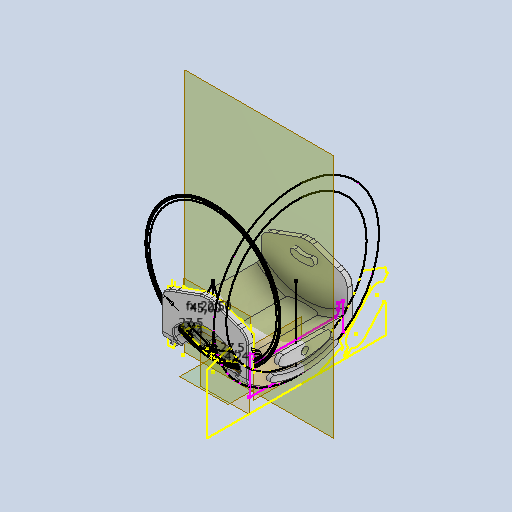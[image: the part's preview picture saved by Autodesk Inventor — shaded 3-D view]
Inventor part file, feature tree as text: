
AUTODESK INVENTOR PART (.ipt)
format: ipt  version: 2022 (Build 260153000, 153)  size: 1,173,504 bytes
history: native  units: mm
features: reference x42, other x22, extrude x21, sketch x20, projected_geometry x20, fillet x14, mirror x1
ambient origin geometry x8: Origin, YZ Plane, XZ Plane, XY Plane, X Axis, Y Axis, Z Axis, Center Point
bodies: Body1 (feature_tree)
feature tree (140):
  other  "Твердое тело1"
  extrude  "Выдавливание1"  Depth=1.2mm
  sketch  "Эскиз2"
  other  "РабПлоскость11"
  extrude  "Выдавливание2"  Depth=3.490659mm
  sketch  "Эскиз4"
  extrude  "Выдавливание3"  Depth=3.490659mm
  extrude  "Выдавливание4"  Depth=0.2mm
  other  "РабПлоскость2"
  other  "РабПлоскость3"
  extrude  "Выдавливание5"  Depth=2.7mm TaperAngle=0.0deg
  extrude  "Выдавливание6"  Depth=0.05mm
  fillet  "Сопряжение6"  [1 undecoded]
  fillet  "Сопряжение8"  [1 undecoded]
  extrude  "Выдавливание9"  Depth=1.8mm TaperAngle=0.0deg
  other  "РабПлоскость6"
  extrude  "Выдавливание11"  Depth=1.0mm
  other  "РабПлоскость5"
  sketch  "Эскиз15"
  extrude  "Выдавливание12"  TaperAngle=45.0deg  [1 undecoded]
  other  "РабПлоскость7"
  extrude  "Выдавливание13"  TaperAngle=22.5deg  [1 undecoded]
  extrude  "Выдавливание14"  Depth=27.5mm
  extrude  "Выдавливание15"  Depth=27.5mm
  extrude  "Выдавливание16"  Depth=4.24mm
  sketch  "Эскиз22"
  other  "РабПлоскость4"
  extrude  "Выдавливание17"  Depth=4.24mm
  extrude  "Выдавливание18"  Depth=42.5mm TaperAngle=0.0deg
  fillet  "Сопряжение12"  Radius=2.7mm
  other  "РабПлоскость8"
  fillet  "Сопряжение13"  Radius=0.2mm
  extrude  "Выдавливание20"  Depth=8.0mm TaperAngle=0.0deg
  fillet  "Сопряжение14"  Radius=4.0mm
  fillet  "Сопряжение15"  Radius=0.5mm
  other  "РабПлоскость9"
  mirror  "Зеркальное отражение1"
  extrude  "Выдавливание21"  Depth=4.363323mm
  fillet  "Сопряжение17"  Radius=4.363323mm
  fillet  "Сопряжение20"  Radius=0.3mm
  fillet  "Сопряжение21"  Radius=1.0mm
  extrude  "Выдавливание25"  Depth=0.8mm
  extrude  "Выдавливание26"  Depth=5.0mm
  fillet  "Сопряжение23"  Radius=10.0mm
  fillet  "Сопряжение24"  Radius=40.0mm
  fillet  "Сопряжение27"  Radius=40.0mm
  fillet  "Сопряжение28"  Radius=4.3mm
  extrude  "Выдавливание27"  Depth=1.3mm TaperAngle=0.0deg
  fillet  "Сопряжение29"  Radius=1.8mm
  extrude  "Выдавливание28"  Depth=2.0mm TaperAngle=0.0deg
  sketch  "Эскиз1"
  reference  "Ссылка1"
  reference  "Ссылка2"
  reference  "Ссылка3"
  reference  "Ссылка4"
  reference  "Ссылка5"
  reference  "Ссылка6"
  reference  "Ссылка7"
  reference  "Ссылка8"
  reference  "Ссылка9"
  reference  "Ссылка10"
  reference  "Ссылка11"
  reference  "Ссылка12"
  reference  "Ссылка13"
  reference  "Ссылка14"
  projected_geometry  "Спроецированная петля1"
  reference  "Ссылка15"
  reference  "Ссылка16"
  reference  "Ссылка17"
  reference  "Ссылка18"
  reference  "Ссылка19"
  reference  "Ссылка20"
  sketch  "Эскиз5"
  projected_geometry  "Спроецированная петля2"
  sketch  "Эскиз6"
  projected_geometry  "Спроецированная петля3"
  sketch  "Эскиз8"
  reference  "Ссылка29"
  reference  "Ссылка31"
  projected_geometry  "Спроецированная петля5"
  projected_geometry  "Спроецированная петля6"
  reference  "Ссылка32"
  reference  "Ссылка33"
  sketch  "Эскиз9"
  projected_geometry  "Спроецированная петля7"
  sketch  "Эскиз12"
  projected_geometry  "Спроецированная петля10"
  sketch  "Эскиз16"
  sketch  "Эскиз17"
  projected_geometry  "Спроецированная петля13"
  projected_geometry  "Спроецированная петля14"
  sketch  "Эскиз18"
  sketch  "Эскиз19"
  reference  "Ссылка50"
  reference  "Ссылка51"
  reference  "Ссылка52"
  reference  "Ссылка53"
  reference  "Ссылка54"
  reference  "Ссылка55"
  projected_geometry  "Спроецированная петля17"
  projected_geometry  "Спроецированная петля18"
  projected_geometry  "Спроецированная петля19"
  sketch  "Эскиз25"
  reference  "Ссылка59"
  other  "РабПлоскость10"
  sketch  "Эскиз26"
  reference  "Ссылка61"
  projected_geometry  "Спроецированная петля20"
  projected_geometry  "Спроецированная петля21"
  reference  "Ссылка62"
  reference  "Ссылка63"
  projected_geometry  "Спроецированная петля27"
  reference  "Ссылка67"
  reference  "Ссылка68"
  projected_geometry  "Спроецированная петля29"
  reference  "Ссылка69"
  projected_geometry  "Спроецированная петля30"
  reference  "Ссылка70"
  projected_geometry  "Спроецированная петля31"
  sketch  "Эскиз30"
  projected_geometry  "Спроецированная петля34"
  reference  "Ссылка71"
  sketch  "Эскиз31"
  projected_geometry  "Спроецированная петля35"
  sketch  "Эскиз32"
  reference  "Ссылка72"
  sketch  "Эскиз33"
  reference  "Ссылка73"
  reference  "Ссылка74"
  other  "<userpath>\Documents\Git\MZCAT_2024\MZCAT_2.iam"
  other  "MZCAT_2.iam"
  other  "lidar_base:1"
  other  "shatun_lidar:1"
  other  "OCS-D008 B:3"
  other  "CAT_protector:1"
  other  "OCS-D008 B:2"
  other  "<userpath>\Documents\Git\MZCAT_2024\MZCAT_4.iam"
  other  "MZCAT_4.iam"
  other  "LD19:1"
  other  "lidar_krestovina_base:1"
note: 4 required parameter values undecoded (feature->parameter linkage not recoverable at this tier; creation-order binding heuristic only, values carry confidence <= 0.55)
